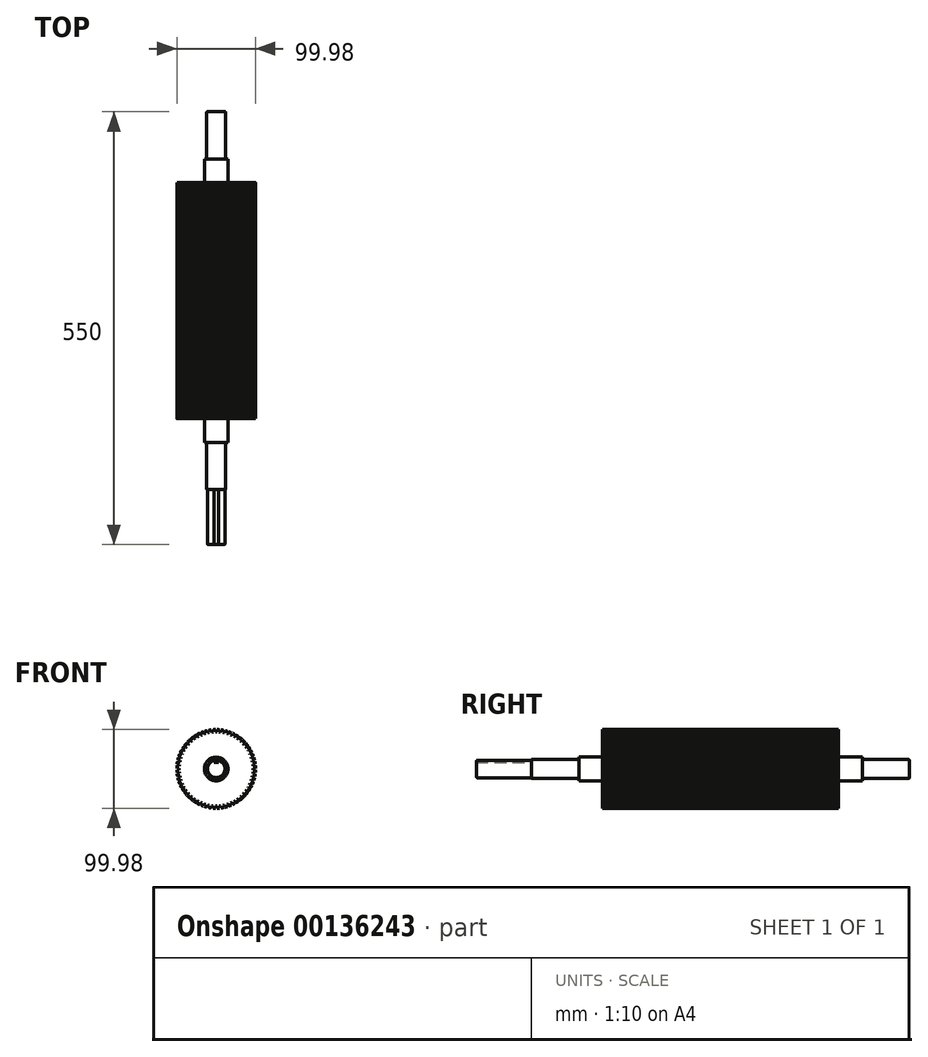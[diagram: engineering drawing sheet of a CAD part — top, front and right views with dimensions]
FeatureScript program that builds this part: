
annotation { "Feature Type Name" : "Feature", "Feature Type Description" : "" }
export const myFeature = defineFeature(function(context is Context, id is Id, definition is map)
    precondition{}
    {
        {
            var Q0;
            Q0=qCreatedBy(makeId("Front.planeOp"),FACE);
            var sketch = newSketch(context, id + "F0", { "sketchPlane" : qUnion([Q0])});
            skCircle(sketch, "E0", {"center": v(0, 0) * mm, "radius": 50 * mm});
            skLineSegment(sketch, "E1.bottom", {"start": v(-1, 50) * mm, "end": v(0, 50) * mm});
            skLineSegment(sketch, "E1.top", {"start": v(-1, 47) * mm, "end": v(0, 47) * mm});
            skLineSegment(sketch, "E1.left", {"start": v(-1, 50) * mm, "end": v(-1, 47) * mm});
            skLineSegment(sketch, "E2.MirrorCS", {"start": v(1, 50) * mm, "end": v(1, 47) * mm});
            skLineSegment(sketch, "E3.MirrorCS", {"start": v(1, 47) * mm, "end": v(0, 47) * mm});
            skPoint(sketch, "E4.MirrorCS.end.orphan", {"position": v(-2, 47) * mm});
            skPoint(sketch, "E4.MirrorCS.start.orphan", {"position": v(-1, 47) * mm});
            skLineSegment(sketch, "E5.1.0", {"start": v(-6.22, 49.62) * mm, "end": v(-5.9, 46.64) * mm});
            skLineSegment(sketch, "E5.1.1", {"start": v(-5.9, 46.64) * mm, "end": v(-4.91, 46.74) * mm});
            skLineSegment(sketch, "E5.1.2", {"start": v(-3.92, 46.85) * mm, "end": v(-4.91, 46.74) * mm});
            skLineSegment(sketch, "E5.1.3", {"start": v(-4.23, 49.83) * mm, "end": v(-3.92, 46.85) * mm});
            skLineSegment(sketch, "E5.2.0", {"start": v(-11.37, 48.7) * mm, "end": v(-10.75, 45.77) * mm});
            skLineSegment(sketch, "E5.2.1", {"start": v(-10.75, 45.77) * mm, "end": v(-9.77, 45.97) * mm});
            skLineSegment(sketch, "E5.2.2", {"start": v(-8.8, 46.18) * mm, "end": v(-9.77, 45.97) * mm});
            skLineSegment(sketch, "E5.2.3", {"start": v(-9.42, 49.12) * mm, "end": v(-8.8, 46.18) * mm});
            skLineSegment(sketch, "E5.3.0", {"start": v(-16.4, 47.24) * mm, "end": v(-15.47, 44.4) * mm});
            skLineSegment(sketch, "E5.3.1", {"start": v(-15.47, 44.4) * mm, "end": v(-14.52, 44.7) * mm});
            skLineSegment(sketch, "E5.3.2", {"start": v(-13.57, 45) * mm, "end": v(-14.52, 44.7) * mm});
            skLineSegment(sketch, "E5.3.3", {"start": v(-14.5, 47.86) * mm, "end": v(-13.57, 45) * mm});
            skLineSegment(sketch, "E5.4.0", {"start": v(-21.25, 45.27) * mm, "end": v(-20.03, 42.53) * mm});
            skLineSegment(sketch, "E5.4.1", {"start": v(-20.03, 42.53) * mm, "end": v(-19.12, 42.94) * mm});
            skLineSegment(sketch, "E5.4.2", {"start": v(-18.2, 43.34) * mm, "end": v(-19.12, 42.94) * mm});
            skLineSegment(sketch, "E5.4.3", {"start": v(-19.42, 46.08) * mm, "end": v(-18.2, 43.34) * mm});
            skLineSegment(sketch, "E5.5.0", {"start": v(-25.87, 42.8) * mm, "end": v(-24.37, 40.2) * mm});
            skLineSegment(sketch, "E5.5.1", {"start": v(-24.37, 40.2) * mm, "end": v(-23.5, 40.7) * mm});
            skLineSegment(sketch, "E5.5.2", {"start": v(-22.63, 41.2) * mm, "end": v(-23.5, 40.7) * mm});
            skLineSegment(sketch, "E5.5.3", {"start": v(-24.13, 43.8) * mm, "end": v(-22.63, 41.2) * mm});
            skLineSegment(sketch, "E5.6.0", {"start": v(-30.2, 39.86) * mm, "end": v(-28.43, 37.44) * mm});
            skLineSegment(sketch, "E5.6.1", {"start": v(-28.43, 37.44) * mm, "end": v(-27.63, 38.02) * mm});
            skLineSegment(sketch, "E5.6.2", {"start": v(-26.82, 38.61) * mm, "end": v(-27.63, 38.02) * mm});
            skLineSegment(sketch, "E5.6.3", {"start": v(-28.58, 41.04) * mm, "end": v(-26.82, 38.61) * mm});
            skLineSegment(sketch, "E5.7.0", {"start": v(-34.2, 36.49) * mm, "end": v(-32.2, 34.26) * mm});
            skLineSegment(sketch, "E5.7.1", {"start": v(-32.2, 34.26) * mm, "end": v(-31.45, 34.93) * mm});
            skLineSegment(sketch, "E5.7.2", {"start": v(-30.7, 35.6) * mm, "end": v(-31.45, 34.93) * mm});
            skLineSegment(sketch, "E5.7.3", {"start": v(-32.71, 37.83) * mm, "end": v(-30.7, 35.6) * mm});
            skLineSegment(sketch, "E5.8.0", {"start": v(-37.83, 32.71) * mm, "end": v(-35.6, 30.7) * mm});
            skLineSegment(sketch, "E5.8.1", {"start": v(-35.6, 30.7) * mm, "end": v(-34.93, 31.45) * mm});
            skLineSegment(sketch, "E5.8.2", {"start": v(-34.26, 32.2) * mm, "end": v(-34.93, 31.45) * mm});
            skLineSegment(sketch, "E5.8.3", {"start": v(-36.49, 34.2) * mm, "end": v(-34.26, 32.2) * mm});
            skLineSegment(sketch, "E5.9.0", {"start": v(-41.04, 28.58) * mm, "end": v(-38.61, 26.82) * mm});
            skLineSegment(sketch, "E5.9.1", {"start": v(-38.61, 26.82) * mm, "end": v(-38.02, 27.63) * mm});
            skLineSegment(sketch, "E5.9.2", {"start": v(-37.44, 28.43) * mm, "end": v(-38.02, 27.63) * mm});
            skLineSegment(sketch, "E5.9.3", {"start": v(-39.86, 30.2) * mm, "end": v(-37.44, 28.43) * mm});
            skLineSegment(sketch, "E5.10.0", {"start": v(-43.8, 24.13) * mm, "end": v(-41.2, 22.63) * mm});
            skLineSegment(sketch, "E5.10.1", {"start": v(-41.2, 22.63) * mm, "end": v(-40.7, 23.5) * mm});
            skLineSegment(sketch, "E5.10.2", {"start": v(-40.2, 24.37) * mm, "end": v(-40.7, 23.5) * mm});
            skLineSegment(sketch, "E5.10.3", {"start": v(-42.8, 25.87) * mm, "end": v(-40.2, 24.37) * mm});
            skLineSegment(sketch, "E5.11.0", {"start": v(-46.08, 19.42) * mm, "end": v(-43.34, 18.2) * mm});
            skLineSegment(sketch, "E5.11.1", {"start": v(-43.34, 18.2) * mm, "end": v(-42.94, 19.12) * mm});
            skLineSegment(sketch, "E5.11.2", {"start": v(-42.53, 20.03) * mm, "end": v(-42.94, 19.12) * mm});
            skLineSegment(sketch, "E5.11.3", {"start": v(-45.27, 21.25) * mm, "end": v(-42.53, 20.03) * mm});
            skLineSegment(sketch, "E5.12.0", {"start": v(-47.86, 14.5) * mm, "end": v(-45, 13.57) * mm});
            skLineSegment(sketch, "E5.12.1", {"start": v(-45, 13.57) * mm, "end": v(-44.7, 14.52) * mm});
            skLineSegment(sketch, "E5.12.2", {"start": v(-44.4, 15.47) * mm, "end": v(-44.7, 14.52) * mm});
            skLineSegment(sketch, "E5.12.3", {"start": v(-47.24, 16.4) * mm, "end": v(-44.4, 15.47) * mm});
            skLineSegment(sketch, "E5.13.0", {"start": v(-49.12, 9.42) * mm, "end": v(-46.18, 8.8) * mm});
            skLineSegment(sketch, "E5.13.1", {"start": v(-46.18, 8.8) * mm, "end": v(-45.97, 9.77) * mm});
            skLineSegment(sketch, "E5.13.2", {"start": v(-45.77, 10.75) * mm, "end": v(-45.97, 9.77) * mm});
            skLineSegment(sketch, "E5.13.3", {"start": v(-48.7, 11.37) * mm, "end": v(-45.77, 10.75) * mm});
            skLineSegment(sketch, "E5.14.0", {"start": v(-49.83, 4.23) * mm, "end": v(-46.85, 3.92) * mm});
            skLineSegment(sketch, "E5.14.1", {"start": v(-46.85, 3.92) * mm, "end": v(-46.74, 4.91) * mm});
            skLineSegment(sketch, "E5.14.2", {"start": v(-46.64, 5.9) * mm, "end": v(-46.74, 4.91) * mm});
            skLineSegment(sketch, "E5.14.3", {"start": v(-49.62, 6.22) * mm, "end": v(-46.64, 5.9) * mm});
            skLineSegment(sketch, "E5.15.0", {"start": v(-50, -1) * mm, "end": v(-47, -1) * mm});
            skLineSegment(sketch, "E5.15.1", {"start": v(-47, -1) * mm, "end": v(-47, 0) * mm});
            skLineSegment(sketch, "E5.15.2", {"start": v(-47, 1) * mm, "end": v(-47, 0) * mm});
            skLineSegment(sketch, "E5.15.3", {"start": v(-50, 1) * mm, "end": v(-47, 1) * mm});
            skLineSegment(sketch, "E5.16.0", {"start": v(-49.62, -6.22) * mm, "end": v(-46.64, -5.9) * mm});
            skLineSegment(sketch, "E5.16.1", {"start": v(-46.64, -5.9) * mm, "end": v(-46.74, -4.91) * mm});
            skLineSegment(sketch, "E5.16.2", {"start": v(-46.85, -3.92) * mm, "end": v(-46.74, -4.91) * mm});
            skLineSegment(sketch, "E5.16.3", {"start": v(-49.83, -4.23) * mm, "end": v(-46.85, -3.92) * mm});
            skLineSegment(sketch, "E5.17.0", {"start": v(-48.7, -11.37) * mm, "end": v(-45.77, -10.75) * mm});
            skLineSegment(sketch, "E5.17.1", {"start": v(-45.77, -10.75) * mm, "end": v(-45.97, -9.77) * mm});
            skLineSegment(sketch, "E5.17.2", {"start": v(-46.18, -8.8) * mm, "end": v(-45.97, -9.77) * mm});
            skLineSegment(sketch, "E5.17.3", {"start": v(-49.12, -9.42) * mm, "end": v(-46.18, -8.8) * mm});
            skLineSegment(sketch, "E5.18.0", {"start": v(-47.24, -16.4) * mm, "end": v(-44.4, -15.47) * mm});
            skLineSegment(sketch, "E5.18.1", {"start": v(-44.4, -15.47) * mm, "end": v(-44.7, -14.52) * mm});
            skLineSegment(sketch, "E5.18.2", {"start": v(-45, -13.57) * mm, "end": v(-44.7, -14.52) * mm});
            skLineSegment(sketch, "E5.18.3", {"start": v(-47.86, -14.5) * mm, "end": v(-45, -13.57) * mm});
            skLineSegment(sketch, "E5.19.0", {"start": v(-45.27, -21.25) * mm, "end": v(-42.53, -20.03) * mm});
            skLineSegment(sketch, "E5.19.1", {"start": v(-42.53, -20.03) * mm, "end": v(-42.94, -19.12) * mm});
            skLineSegment(sketch, "E5.19.2", {"start": v(-43.34, -18.2) * mm, "end": v(-42.94, -19.12) * mm});
            skLineSegment(sketch, "E5.19.3", {"start": v(-46.08, -19.42) * mm, "end": v(-43.34, -18.2) * mm});
            skLineSegment(sketch, "E5.20.0", {"start": v(-42.8, -25.87) * mm, "end": v(-40.2, -24.37) * mm});
            skLineSegment(sketch, "E5.20.1", {"start": v(-40.2, -24.37) * mm, "end": v(-40.7, -23.5) * mm});
            skLineSegment(sketch, "E5.20.2", {"start": v(-41.2, -22.63) * mm, "end": v(-40.7, -23.5) * mm});
            skLineSegment(sketch, "E5.20.3", {"start": v(-43.8, -24.13) * mm, "end": v(-41.2, -22.63) * mm});
            skLineSegment(sketch, "E5.21.0", {"start": v(-39.86, -30.2) * mm, "end": v(-37.44, -28.43) * mm});
            skLineSegment(sketch, "E5.21.1", {"start": v(-37.44, -28.43) * mm, "end": v(-38.02, -27.63) * mm});
            skLineSegment(sketch, "E5.21.2", {"start": v(-38.61, -26.82) * mm, "end": v(-38.02, -27.63) * mm});
            skLineSegment(sketch, "E5.21.3", {"start": v(-41.04, -28.58) * mm, "end": v(-38.61, -26.82) * mm});
            skLineSegment(sketch, "E5.22.0", {"start": v(-36.49, -34.2) * mm, "end": v(-34.26, -32.2) * mm});
            skLineSegment(sketch, "E5.22.1", {"start": v(-34.26, -32.2) * mm, "end": v(-34.93, -31.45) * mm});
            skLineSegment(sketch, "E5.22.2", {"start": v(-35.6, -30.7) * mm, "end": v(-34.93, -31.45) * mm});
            skLineSegment(sketch, "E5.22.3", {"start": v(-37.83, -32.71) * mm, "end": v(-35.6, -30.7) * mm});
            skLineSegment(sketch, "E5.23.0", {"start": v(-32.71, -37.83) * mm, "end": v(-30.7, -35.6) * mm});
            skLineSegment(sketch, "E5.23.1", {"start": v(-30.7, -35.6) * mm, "end": v(-31.45, -34.93) * mm});
            skLineSegment(sketch, "E5.23.2", {"start": v(-32.2, -34.26) * mm, "end": v(-31.45, -34.93) * mm});
            skLineSegment(sketch, "E5.23.3", {"start": v(-34.2, -36.49) * mm, "end": v(-32.2, -34.26) * mm});
            skLineSegment(sketch, "E5.24.0", {"start": v(-28.58, -41.04) * mm, "end": v(-26.82, -38.61) * mm});
            skLineSegment(sketch, "E5.24.1", {"start": v(-26.82, -38.61) * mm, "end": v(-27.63, -38.02) * mm});
            skLineSegment(sketch, "E5.24.2", {"start": v(-28.43, -37.44) * mm, "end": v(-27.63, -38.02) * mm});
            skLineSegment(sketch, "E5.24.3", {"start": v(-30.2, -39.86) * mm, "end": v(-28.43, -37.44) * mm});
            skLineSegment(sketch, "E5.25.0", {"start": v(-24.13, -43.8) * mm, "end": v(-22.63, -41.2) * mm});
            skLineSegment(sketch, "E5.25.1", {"start": v(-22.63, -41.2) * mm, "end": v(-23.5, -40.7) * mm});
            skLineSegment(sketch, "E5.25.2", {"start": v(-24.37, -40.2) * mm, "end": v(-23.5, -40.7) * mm});
            skLineSegment(sketch, "E5.25.3", {"start": v(-25.87, -42.8) * mm, "end": v(-24.37, -40.2) * mm});
            skLineSegment(sketch, "E5.26.0", {"start": v(-19.42, -46.08) * mm, "end": v(-18.2, -43.34) * mm});
            skLineSegment(sketch, "E5.26.1", {"start": v(-18.2, -43.34) * mm, "end": v(-19.12, -42.94) * mm});
            skLineSegment(sketch, "E5.26.2", {"start": v(-20.03, -42.53) * mm, "end": v(-19.12, -42.94) * mm});
            skLineSegment(sketch, "E5.26.3", {"start": v(-21.25, -45.27) * mm, "end": v(-20.03, -42.53) * mm});
            skLineSegment(sketch, "E5.27.0", {"start": v(-14.5, -47.86) * mm, "end": v(-13.57, -45) * mm});
            skLineSegment(sketch, "E5.27.1", {"start": v(-13.57, -45) * mm, "end": v(-14.52, -44.7) * mm});
            skLineSegment(sketch, "E5.27.2", {"start": v(-15.47, -44.4) * mm, "end": v(-14.52, -44.7) * mm});
            skLineSegment(sketch, "E5.27.3", {"start": v(-16.4, -47.24) * mm, "end": v(-15.47, -44.4) * mm});
            skLineSegment(sketch, "E5.28.0", {"start": v(-9.42, -49.12) * mm, "end": v(-8.8, -46.18) * mm});
            skLineSegment(sketch, "E5.28.1", {"start": v(-8.8, -46.18) * mm, "end": v(-9.77, -45.97) * mm});
            skLineSegment(sketch, "E5.28.2", {"start": v(-10.75, -45.77) * mm, "end": v(-9.77, -45.97) * mm});
            skLineSegment(sketch, "E5.28.3", {"start": v(-11.37, -48.7) * mm, "end": v(-10.75, -45.77) * mm});
            skLineSegment(sketch, "E5.29.0", {"start": v(-4.23, -49.83) * mm, "end": v(-3.92, -46.85) * mm});
            skLineSegment(sketch, "E5.29.1", {"start": v(-3.92, -46.85) * mm, "end": v(-4.91, -46.74) * mm});
            skLineSegment(sketch, "E5.29.2", {"start": v(-5.9, -46.64) * mm, "end": v(-4.91, -46.74) * mm});
            skLineSegment(sketch, "E5.29.3", {"start": v(-6.22, -49.62) * mm, "end": v(-5.9, -46.64) * mm});
            skLineSegment(sketch, "E5.30.0", {"start": v(1, -50) * mm, "end": v(1, -47) * mm});
            skLineSegment(sketch, "E5.30.1", {"start": v(1, -47) * mm, "end": v(0, -47) * mm});
            skLineSegment(sketch, "E5.30.2", {"start": v(-1, -47) * mm, "end": v(0, -47) * mm});
            skLineSegment(sketch, "E5.30.3", {"start": v(-1, -50) * mm, "end": v(-1, -47) * mm});
            skLineSegment(sketch, "E5.31.0", {"start": v(6.22, -49.62) * mm, "end": v(5.9, -46.64) * mm});
            skLineSegment(sketch, "E5.31.1", {"start": v(5.9, -46.64) * mm, "end": v(4.91, -46.74) * mm});
            skLineSegment(sketch, "E5.31.2", {"start": v(3.92, -46.85) * mm, "end": v(4.91, -46.74) * mm});
            skLineSegment(sketch, "E5.31.3", {"start": v(4.23, -49.83) * mm, "end": v(3.92, -46.85) * mm});
            skLineSegment(sketch, "E5.32.0", {"start": v(11.37, -48.7) * mm, "end": v(10.75, -45.77) * mm});
            skLineSegment(sketch, "E5.32.1", {"start": v(10.75, -45.77) * mm, "end": v(9.77, -45.97) * mm});
            skLineSegment(sketch, "E5.32.2", {"start": v(8.8, -46.18) * mm, "end": v(9.77, -45.97) * mm});
            skLineSegment(sketch, "E5.32.3", {"start": v(9.42, -49.12) * mm, "end": v(8.8, -46.18) * mm});
            skLineSegment(sketch, "E5.33.0", {"start": v(16.4, -47.24) * mm, "end": v(15.47, -44.4) * mm});
            skLineSegment(sketch, "E5.33.1", {"start": v(15.47, -44.4) * mm, "end": v(14.52, -44.7) * mm});
            skLineSegment(sketch, "E5.33.2", {"start": v(13.57, -45) * mm, "end": v(14.52, -44.7) * mm});
            skLineSegment(sketch, "E5.33.3", {"start": v(14.5, -47.86) * mm, "end": v(13.57, -45) * mm});
            skLineSegment(sketch, "E5.34.0", {"start": v(21.25, -45.27) * mm, "end": v(20.03, -42.53) * mm});
            skLineSegment(sketch, "E5.34.1", {"start": v(20.03, -42.53) * mm, "end": v(19.12, -42.94) * mm});
            skLineSegment(sketch, "E5.34.2", {"start": v(18.2, -43.34) * mm, "end": v(19.12, -42.94) * mm});
            skLineSegment(sketch, "E5.34.3", {"start": v(19.42, -46.08) * mm, "end": v(18.2, -43.34) * mm});
            skLineSegment(sketch, "E5.35.0", {"start": v(25.87, -42.8) * mm, "end": v(24.37, -40.2) * mm});
            skLineSegment(sketch, "E5.35.1", {"start": v(24.37, -40.2) * mm, "end": v(23.5, -40.7) * mm});
            skLineSegment(sketch, "E5.35.2", {"start": v(22.63, -41.2) * mm, "end": v(23.5, -40.7) * mm});
            skLineSegment(sketch, "E5.35.3", {"start": v(24.13, -43.8) * mm, "end": v(22.63, -41.2) * mm});
            skLineSegment(sketch, "E5.36.0", {"start": v(30.2, -39.86) * mm, "end": v(28.43, -37.44) * mm});
            skLineSegment(sketch, "E5.36.1", {"start": v(28.43, -37.44) * mm, "end": v(27.63, -38.02) * mm});
            skLineSegment(sketch, "E5.36.2", {"start": v(26.82, -38.61) * mm, "end": v(27.63, -38.02) * mm});
            skLineSegment(sketch, "E5.36.3", {"start": v(28.58, -41.04) * mm, "end": v(26.82, -38.61) * mm});
            skLineSegment(sketch, "E5.37.0", {"start": v(34.2, -36.49) * mm, "end": v(32.2, -34.26) * mm});
            skLineSegment(sketch, "E5.37.1", {"start": v(32.2, -34.26) * mm, "end": v(31.45, -34.93) * mm});
            skLineSegment(sketch, "E5.37.2", {"start": v(30.7, -35.6) * mm, "end": v(31.45, -34.93) * mm});
            skLineSegment(sketch, "E5.37.3", {"start": v(32.71, -37.83) * mm, "end": v(30.7, -35.6) * mm});
            skLineSegment(sketch, "E5.38.0", {"start": v(37.83, -32.71) * mm, "end": v(35.6, -30.7) * mm});
            skLineSegment(sketch, "E5.38.1", {"start": v(35.6, -30.7) * mm, "end": v(34.93, -31.45) * mm});
            skLineSegment(sketch, "E5.38.2", {"start": v(34.26, -32.2) * mm, "end": v(34.93, -31.45) * mm});
            skLineSegment(sketch, "E5.38.3", {"start": v(36.49, -34.2) * mm, "end": v(34.26, -32.2) * mm});
            skLineSegment(sketch, "E5.39.0", {"start": v(41.04, -28.58) * mm, "end": v(38.61, -26.82) * mm});
            skLineSegment(sketch, "E5.39.1", {"start": v(38.61, -26.82) * mm, "end": v(38.02, -27.63) * mm});
            skLineSegment(sketch, "E5.39.2", {"start": v(37.44, -28.43) * mm, "end": v(38.02, -27.63) * mm});
            skLineSegment(sketch, "E5.39.3", {"start": v(39.86, -30.2) * mm, "end": v(37.44, -28.43) * mm});
            skLineSegment(sketch, "E5.40.0", {"start": v(43.8, -24.13) * mm, "end": v(41.2, -22.63) * mm});
            skLineSegment(sketch, "E5.40.1", {"start": v(41.2, -22.63) * mm, "end": v(40.7, -23.5) * mm});
            skLineSegment(sketch, "E5.40.2", {"start": v(40.2, -24.37) * mm, "end": v(40.7, -23.5) * mm});
            skLineSegment(sketch, "E5.40.3", {"start": v(42.8, -25.87) * mm, "end": v(40.2, -24.37) * mm});
            skLineSegment(sketch, "E5.41.0", {"start": v(46.08, -19.42) * mm, "end": v(43.34, -18.2) * mm});
            skLineSegment(sketch, "E5.41.1", {"start": v(43.34, -18.2) * mm, "end": v(42.94, -19.12) * mm});
            skLineSegment(sketch, "E5.41.2", {"start": v(42.53, -20.03) * mm, "end": v(42.94, -19.12) * mm});
            skLineSegment(sketch, "E5.41.3", {"start": v(45.27, -21.25) * mm, "end": v(42.53, -20.03) * mm});
            skLineSegment(sketch, "E5.42.0", {"start": v(47.86, -14.5) * mm, "end": v(45, -13.57) * mm});
            skLineSegment(sketch, "E5.42.1", {"start": v(45, -13.57) * mm, "end": v(44.7, -14.52) * mm});
            skLineSegment(sketch, "E5.42.2", {"start": v(44.4, -15.47) * mm, "end": v(44.7, -14.52) * mm});
            skLineSegment(sketch, "E5.42.3", {"start": v(47.24, -16.4) * mm, "end": v(44.4, -15.47) * mm});
            skLineSegment(sketch, "E5.43.0", {"start": v(49.12, -9.42) * mm, "end": v(46.18, -8.8) * mm});
            skLineSegment(sketch, "E5.43.1", {"start": v(46.18, -8.8) * mm, "end": v(45.97, -9.77) * mm});
            skLineSegment(sketch, "E5.43.2", {"start": v(45.77, -10.75) * mm, "end": v(45.97, -9.77) * mm});
            skLineSegment(sketch, "E5.43.3", {"start": v(48.7, -11.37) * mm, "end": v(45.77, -10.75) * mm});
            skLineSegment(sketch, "E5.44.0", {"start": v(49.83, -4.23) * mm, "end": v(46.85, -3.92) * mm});
            skLineSegment(sketch, "E5.44.1", {"start": v(46.85, -3.92) * mm, "end": v(46.74, -4.91) * mm});
            skLineSegment(sketch, "E5.44.2", {"start": v(46.64, -5.9) * mm, "end": v(46.74, -4.91) * mm});
            skLineSegment(sketch, "E5.44.3", {"start": v(49.62, -6.22) * mm, "end": v(46.64, -5.9) * mm});
            skLineSegment(sketch, "E5.45.0", {"start": v(50, 1) * mm, "end": v(47, 1) * mm});
            skLineSegment(sketch, "E5.45.1", {"start": v(47, 1) * mm, "end": v(47, 0) * mm});
            skLineSegment(sketch, "E5.45.2", {"start": v(47, -1) * mm, "end": v(47, 0) * mm});
            skLineSegment(sketch, "E5.45.3", {"start": v(50, -1) * mm, "end": v(47, -1) * mm});
            skLineSegment(sketch, "E5.46.0", {"start": v(49.62, 6.22) * mm, "end": v(46.64, 5.9) * mm});
            skLineSegment(sketch, "E5.46.1", {"start": v(46.64, 5.9) * mm, "end": v(46.74, 4.91) * mm});
            skLineSegment(sketch, "E5.46.2", {"start": v(46.85, 3.92) * mm, "end": v(46.74, 4.91) * mm});
            skLineSegment(sketch, "E5.46.3", {"start": v(49.83, 4.23) * mm, "end": v(46.85, 3.92) * mm});
            skLineSegment(sketch, "E5.47.0", {"start": v(48.7, 11.37) * mm, "end": v(45.77, 10.75) * mm});
            skLineSegment(sketch, "E5.47.1", {"start": v(45.77, 10.75) * mm, "end": v(45.97, 9.77) * mm});
            skLineSegment(sketch, "E5.47.2", {"start": v(46.18, 8.8) * mm, "end": v(45.97, 9.77) * mm});
            skLineSegment(sketch, "E5.47.3", {"start": v(49.12, 9.42) * mm, "end": v(46.18, 8.8) * mm});
            skLineSegment(sketch, "E5.48.0", {"start": v(47.24, 16.4) * mm, "end": v(44.4, 15.47) * mm});
            skLineSegment(sketch, "E5.48.1", {"start": v(44.4, 15.47) * mm, "end": v(44.7, 14.52) * mm});
            skLineSegment(sketch, "E5.48.2", {"start": v(45, 13.57) * mm, "end": v(44.7, 14.52) * mm});
            skLineSegment(sketch, "E5.48.3", {"start": v(47.86, 14.5) * mm, "end": v(45, 13.57) * mm});
            skLineSegment(sketch, "E5.49.0", {"start": v(45.27, 21.25) * mm, "end": v(42.53, 20.03) * mm});
            skLineSegment(sketch, "E5.49.1", {"start": v(42.53, 20.03) * mm, "end": v(42.94, 19.12) * mm});
            skLineSegment(sketch, "E5.49.2", {"start": v(43.34, 18.2) * mm, "end": v(42.94, 19.12) * mm});
            skLineSegment(sketch, "E5.49.3", {"start": v(46.08, 19.42) * mm, "end": v(43.34, 18.2) * mm});
            skLineSegment(sketch, "E5.50.0", {"start": v(42.8, 25.87) * mm, "end": v(40.2, 24.37) * mm});
            skLineSegment(sketch, "E5.50.1", {"start": v(40.2, 24.37) * mm, "end": v(40.7, 23.5) * mm});
            skLineSegment(sketch, "E5.50.2", {"start": v(41.2, 22.63) * mm, "end": v(40.7, 23.5) * mm});
            skLineSegment(sketch, "E5.50.3", {"start": v(43.8, 24.13) * mm, "end": v(41.2, 22.63) * mm});
            skLineSegment(sketch, "E5.51.0", {"start": v(39.86, 30.2) * mm, "end": v(37.44, 28.43) * mm});
            skLineSegment(sketch, "E5.51.1", {"start": v(37.44, 28.43) * mm, "end": v(38.02, 27.63) * mm});
            skLineSegment(sketch, "E5.51.2", {"start": v(38.61, 26.82) * mm, "end": v(38.02, 27.63) * mm});
            skLineSegment(sketch, "E5.51.3", {"start": v(41.04, 28.58) * mm, "end": v(38.61, 26.82) * mm});
            skLineSegment(sketch, "E5.52.0", {"start": v(36.49, 34.2) * mm, "end": v(34.26, 32.2) * mm});
            skLineSegment(sketch, "E5.52.1", {"start": v(34.26, 32.2) * mm, "end": v(34.93, 31.45) * mm});
            skLineSegment(sketch, "E5.52.2", {"start": v(35.6, 30.7) * mm, "end": v(34.93, 31.45) * mm});
            skLineSegment(sketch, "E5.52.3", {"start": v(37.83, 32.71) * mm, "end": v(35.6, 30.7) * mm});
            skLineSegment(sketch, "E5.53.0", {"start": v(32.71, 37.83) * mm, "end": v(30.7, 35.6) * mm});
            skLineSegment(sketch, "E5.53.1", {"start": v(30.7, 35.6) * mm, "end": v(31.45, 34.93) * mm});
            skLineSegment(sketch, "E5.53.2", {"start": v(32.2, 34.26) * mm, "end": v(31.45, 34.93) * mm});
            skLineSegment(sketch, "E5.53.3", {"start": v(34.2, 36.49) * mm, "end": v(32.2, 34.26) * mm});
            skLineSegment(sketch, "E5.54.0", {"start": v(28.58, 41.04) * mm, "end": v(26.82, 38.61) * mm});
            skLineSegment(sketch, "E5.54.1", {"start": v(26.82, 38.61) * mm, "end": v(27.63, 38.02) * mm});
            skLineSegment(sketch, "E5.54.2", {"start": v(28.43, 37.44) * mm, "end": v(27.63, 38.02) * mm});
            skLineSegment(sketch, "E5.54.3", {"start": v(30.2, 39.86) * mm, "end": v(28.43, 37.44) * mm});
            skLineSegment(sketch, "E5.55.0", {"start": v(24.13, 43.8) * mm, "end": v(22.63, 41.2) * mm});
            skLineSegment(sketch, "E5.55.1", {"start": v(22.63, 41.2) * mm, "end": v(23.5, 40.7) * mm});
            skLineSegment(sketch, "E5.55.2", {"start": v(24.37, 40.2) * mm, "end": v(23.5, 40.7) * mm});
            skLineSegment(sketch, "E5.55.3", {"start": v(25.87, 42.8) * mm, "end": v(24.37, 40.2) * mm});
            skLineSegment(sketch, "E5.56.0", {"start": v(19.42, 46.08) * mm, "end": v(18.2, 43.34) * mm});
            skLineSegment(sketch, "E5.56.1", {"start": v(18.2, 43.34) * mm, "end": v(19.12, 42.94) * mm});
            skLineSegment(sketch, "E5.56.2", {"start": v(20.03, 42.53) * mm, "end": v(19.12, 42.94) * mm});
            skLineSegment(sketch, "E5.56.3", {"start": v(21.25, 45.27) * mm, "end": v(20.03, 42.53) * mm});
            skLineSegment(sketch, "E5.57.0", {"start": v(14.5, 47.86) * mm, "end": v(13.57, 45) * mm});
            skLineSegment(sketch, "E5.57.1", {"start": v(13.57, 45) * mm, "end": v(14.52, 44.7) * mm});
            skLineSegment(sketch, "E5.57.2", {"start": v(15.47, 44.4) * mm, "end": v(14.52, 44.7) * mm});
            skLineSegment(sketch, "E5.57.3", {"start": v(16.4, 47.24) * mm, "end": v(15.47, 44.4) * mm});
            skLineSegment(sketch, "E5.58.0", {"start": v(9.42, 49.12) * mm, "end": v(8.8, 46.18) * mm});
            skLineSegment(sketch, "E5.58.1", {"start": v(8.8, 46.18) * mm, "end": v(9.77, 45.97) * mm});
            skLineSegment(sketch, "E5.58.2", {"start": v(10.75, 45.77) * mm, "end": v(9.77, 45.97) * mm});
            skLineSegment(sketch, "E5.58.3", {"start": v(11.37, 48.7) * mm, "end": v(10.75, 45.77) * mm});
            skLineSegment(sketch, "E5.59.0", {"start": v(4.23, 49.83) * mm, "end": v(3.92, 46.85) * mm});
            skLineSegment(sketch, "E5.59.1", {"start": v(3.92, 46.85) * mm, "end": v(4.91, 46.74) * mm});
            skLineSegment(sketch, "E5.59.2", {"start": v(5.9, 46.64) * mm, "end": v(4.91, 46.74) * mm});
            skLineSegment(sketch, "E5.59.3", {"start": v(6.22, 49.62) * mm, "end": v(5.9, 46.64) * mm});
            skSolve(sketch);
        }
        {
            var Q0;
            {var subQ173=sQuery(id+"F0.wireOp",EDGE,"E1.top");Q0=makeQuery(id+"F0.imprint","IMPRINT",FACE,{"disambiguationData":[TD([[makeQuery(id+"F0.imprint","IMPRINT",EDGE,{"derivedFrom":subQ173}),-1.0]])]});}
            extrude(context, id + "F1", {"entities" : qUnion([Q0]), "endBound" : BoundingType.SYMMETRIC, "depth" : 300 * mm});
        }
        {
            var Q0;
            Q0=makeQuery(id+"F1.opExtrude","CAP_FACE",FACE,{"disambiguationData":[OSD([sQuery(id+"F0.wireOp",EDGE,"E0"),sQuery(id+"F0.wireOp",EDGE,"E1.top"),sQuery(id+"F0.wireOp",EDGE,"E1.left"),sQuery(id+"F0.wireOp",EDGE,"E2.MirrorCS"),sQuery(id+"F0.wireOp",EDGE,"E3.MirrorCS"),sQuery(id+"F0.wireOp",EDGE,"E5.1.0"),sQuery(id+"F0.wireOp",EDGE,"E5.1.1"),sQuery(id+"F0.wireOp",EDGE,"E5.1.2"),sQuery(id+"F0.wireOp",EDGE,"E5.1.3"),sQuery(id+"F0.wireOp",EDGE,"E5.2.0"),sQuery(id+"F0.wireOp",EDGE,"E5.2.1"),sQuery(id+"F0.wireOp",EDGE,"E5.2.2"),sQuery(id+"F0.wireOp",EDGE,"E5.2.3"),sQuery(id+"F0.wireOp",EDGE,"E5.3.0"),sQuery(id+"F0.wireOp",EDGE,"E5.3.1"),sQuery(id+"F0.wireOp",EDGE,"E5.3.2"),sQuery(id+"F0.wireOp",EDGE,"E5.3.3"),sQuery(id+"F0.wireOp",EDGE,"E5.4.0"),sQuery(id+"F0.wireOp",EDGE,"E5.4.1"),sQuery(id+"F0.wireOp",EDGE,"E5.4.2"),sQuery(id+"F0.wireOp",EDGE,"E5.4.3"),sQuery(id+"F0.wireOp",EDGE,"E5.5.0"),sQuery(id+"F0.wireOp",EDGE,"E5.5.1"),sQuery(id+"F0.wireOp",EDGE,"E5.5.2"),sQuery(id+"F0.wireOp",EDGE,"E5.5.3"),sQuery(id+"F0.wireOp",EDGE,"E5.6.0"),sQuery(id+"F0.wireOp",EDGE,"E5.6.1"),sQuery(id+"F0.wireOp",EDGE,"E5.6.2"),sQuery(id+"F0.wireOp",EDGE,"E5.6.3"),sQuery(id+"F0.wireOp",EDGE,"E5.7.0"),sQuery(id+"F0.wireOp",EDGE,"E5.7.1"),sQuery(id+"F0.wireOp",EDGE,"E5.7.2"),sQuery(id+"F0.wireOp",EDGE,"E5.7.3"),sQuery(id+"F0.wireOp",EDGE,"E5.8.0"),sQuery(id+"F0.wireOp",EDGE,"E5.8.1"),sQuery(id+"F0.wireOp",EDGE,"E5.8.2"),sQuery(id+"F0.wireOp",EDGE,"E5.8.3"),sQuery(id+"F0.wireOp",EDGE,"E5.9.0"),sQuery(id+"F0.wireOp",EDGE,"E5.9.1"),sQuery(id+"F0.wireOp",EDGE,"E5.9.2"),sQuery(id+"F0.wireOp",EDGE,"E5.9.3"),sQuery(id+"F0.wireOp",EDGE,"E5.10.0"),sQuery(id+"F0.wireOp",EDGE,"E5.10.1"),sQuery(id+"F0.wireOp",EDGE,"E5.10.2"),sQuery(id+"F0.wireOp",EDGE,"E5.10.3"),sQuery(id+"F0.wireOp",EDGE,"E5.11.0"),sQuery(id+"F0.wireOp",EDGE,"E5.11.1"),sQuery(id+"F0.wireOp",EDGE,"E5.11.2"),sQuery(id+"F0.wireOp",EDGE,"E5.11.3"),sQuery(id+"F0.wireOp",EDGE,"E5.12.0"),sQuery(id+"F0.wireOp",EDGE,"E5.12.1"),sQuery(id+"F0.wireOp",EDGE,"E5.12.2"),sQuery(id+"F0.wireOp",EDGE,"E5.12.3"),sQuery(id+"F0.wireOp",EDGE,"E5.13.0"),sQuery(id+"F0.wireOp",EDGE,"E5.13.1"),sQuery(id+"F0.wireOp",EDGE,"E5.13.2"),sQuery(id+"F0.wireOp",EDGE,"E5.13.3"),sQuery(id+"F0.wireOp",EDGE,"E5.14.0"),sQuery(id+"F0.wireOp",EDGE,"E5.14.1"),sQuery(id+"F0.wireOp",EDGE,"E5.14.2"),sQuery(id+"F0.wireOp",EDGE,"E5.14.3"),sQuery(id+"F0.wireOp",EDGE,"E5.15.0"),sQuery(id+"F0.wireOp",EDGE,"E5.15.1"),sQuery(id+"F0.wireOp",EDGE,"E5.15.2"),sQuery(id+"F0.wireOp",EDGE,"E5.15.3"),sQuery(id+"F0.wireOp",EDGE,"E5.16.0"),sQuery(id+"F0.wireOp",EDGE,"E5.16.1"),sQuery(id+"F0.wireOp",EDGE,"E5.16.2"),sQuery(id+"F0.wireOp",EDGE,"E5.16.3"),sQuery(id+"F0.wireOp",EDGE,"E5.17.0"),sQuery(id+"F0.wireOp",EDGE,"E5.17.1"),sQuery(id+"F0.wireOp",EDGE,"E5.17.2"),sQuery(id+"F0.wireOp",EDGE,"E5.17.3"),sQuery(id+"F0.wireOp",EDGE,"E5.18.0"),sQuery(id+"F0.wireOp",EDGE,"E5.18.1"),sQuery(id+"F0.wireOp",EDGE,"E5.18.2"),sQuery(id+"F0.wireOp",EDGE,"E5.18.3"),sQuery(id+"F0.wireOp",EDGE,"E5.19.0"),sQuery(id+"F0.wireOp",EDGE,"E5.19.1"),sQuery(id+"F0.wireOp",EDGE,"E5.19.2"),sQuery(id+"F0.wireOp",EDGE,"E5.19.3"),sQuery(id+"F0.wireOp",EDGE,"E5.20.0"),sQuery(id+"F0.wireOp",EDGE,"E5.20.1"),sQuery(id+"F0.wireOp",EDGE,"E5.20.2"),sQuery(id+"F0.wireOp",EDGE,"E5.20.3"),sQuery(id+"F0.wireOp",EDGE,"E5.21.0"),sQuery(id+"F0.wireOp",EDGE,"E5.21.1"),sQuery(id+"F0.wireOp",EDGE,"E5.21.2"),sQuery(id+"F0.wireOp",EDGE,"E5.21.3"),sQuery(id+"F0.wireOp",EDGE,"E5.22.0"),sQuery(id+"F0.wireOp",EDGE,"E5.22.1"),sQuery(id+"F0.wireOp",EDGE,"E5.22.2"),sQuery(id+"F0.wireOp",EDGE,"E5.22.3"),sQuery(id+"F0.wireOp",EDGE,"E5.23.0"),sQuery(id+"F0.wireOp",EDGE,"E5.23.1"),sQuery(id+"F0.wireOp",EDGE,"E5.23.2"),sQuery(id+"F0.wireOp",EDGE,"E5.23.3"),sQuery(id+"F0.wireOp",EDGE,"E5.24.0"),sQuery(id+"F0.wireOp",EDGE,"E5.24.1"),sQuery(id+"F0.wireOp",EDGE,"E5.24.2"),sQuery(id+"F0.wireOp",EDGE,"E5.24.3"),sQuery(id+"F0.wireOp",EDGE,"E5.25.0"),sQuery(id+"F0.wireOp",EDGE,"E5.25.1"),sQuery(id+"F0.wireOp",EDGE,"E5.25.2"),sQuery(id+"F0.wireOp",EDGE,"E5.25.3"),sQuery(id+"F0.wireOp",EDGE,"E5.26.0"),sQuery(id+"F0.wireOp",EDGE,"E5.26.1"),sQuery(id+"F0.wireOp",EDGE,"E5.26.2"),sQuery(id+"F0.wireOp",EDGE,"E5.26.3"),sQuery(id+"F0.wireOp",EDGE,"E5.27.0"),sQuery(id+"F0.wireOp",EDGE,"E5.27.1"),sQuery(id+"F0.wireOp",EDGE,"E5.27.2"),sQuery(id+"F0.wireOp",EDGE,"E5.27.3"),sQuery(id+"F0.wireOp",EDGE,"E5.28.0"),sQuery(id+"F0.wireOp",EDGE,"E5.28.1"),sQuery(id+"F0.wireOp",EDGE,"E5.28.2"),sQuery(id+"F0.wireOp",EDGE,"E5.28.3"),sQuery(id+"F0.wireOp",EDGE,"E5.29.0"),sQuery(id+"F0.wireOp",EDGE,"E5.29.1"),sQuery(id+"F0.wireOp",EDGE,"E5.29.2"),sQuery(id+"F0.wireOp",EDGE,"E5.29.3"),sQuery(id+"F0.wireOp",EDGE,"E5.30.0"),sQuery(id+"F0.wireOp",EDGE,"E5.30.1"),sQuery(id+"F0.wireOp",EDGE,"E5.30.2"),sQuery(id+"F0.wireOp",EDGE,"E5.30.3"),sQuery(id+"F0.wireOp",EDGE,"E5.31.0"),sQuery(id+"F0.wireOp",EDGE,"E5.31.1"),sQuery(id+"F0.wireOp",EDGE,"E5.31.2"),sQuery(id+"F0.wireOp",EDGE,"E5.31.3"),sQuery(id+"F0.wireOp",EDGE,"E5.32.0"),sQuery(id+"F0.wireOp",EDGE,"E5.32.1"),sQuery(id+"F0.wireOp",EDGE,"E5.32.2"),sQuery(id+"F0.wireOp",EDGE,"E5.32.3"),sQuery(id+"F0.wireOp",EDGE,"E5.33.0"),sQuery(id+"F0.wireOp",EDGE,"E5.33.1"),sQuery(id+"F0.wireOp",EDGE,"E5.33.2"),sQuery(id+"F0.wireOp",EDGE,"E5.33.3"),sQuery(id+"F0.wireOp",EDGE,"E5.34.0"),sQuery(id+"F0.wireOp",EDGE,"E5.34.1"),sQuery(id+"F0.wireOp",EDGE,"E5.34.2"),sQuery(id+"F0.wireOp",EDGE,"E5.34.3"),sQuery(id+"F0.wireOp",EDGE,"E5.35.0"),sQuery(id+"F0.wireOp",EDGE,"E5.35.1"),sQuery(id+"F0.wireOp",EDGE,"E5.35.2"),sQuery(id+"F0.wireOp",EDGE,"E5.35.3"),sQuery(id+"F0.wireOp",EDGE,"E5.36.0"),sQuery(id+"F0.wireOp",EDGE,"E5.36.1"),sQuery(id+"F0.wireOp",EDGE,"E5.36.2"),sQuery(id+"F0.wireOp",EDGE,"E5.36.3"),sQuery(id+"F0.wireOp",EDGE,"E5.37.0"),sQuery(id+"F0.wireOp",EDGE,"E5.37.1"),sQuery(id+"F0.wireOp",EDGE,"E5.37.2"),sQuery(id+"F0.wireOp",EDGE,"E5.37.3"),sQuery(id+"F0.wireOp",EDGE,"E5.38.0"),sQuery(id+"F0.wireOp",EDGE,"E5.38.1"),sQuery(id+"F0.wireOp",EDGE,"E5.38.2"),sQuery(id+"F0.wireOp",EDGE,"E5.38.3"),sQuery(id+"F0.wireOp",EDGE,"E5.39.0"),sQuery(id+"F0.wireOp",EDGE,"E5.39.1"),sQuery(id+"F0.wireOp",EDGE,"E5.39.2"),sQuery(id+"F0.wireOp",EDGE,"E5.39.3"),sQuery(id+"F0.wireOp",EDGE,"E5.40.0"),sQuery(id+"F0.wireOp",EDGE,"E5.40.1"),sQuery(id+"F0.wireOp",EDGE,"E5.40.2"),sQuery(id+"F0.wireOp",EDGE,"E5.40.3"),sQuery(id+"F0.wireOp",EDGE,"E5.41.0"),sQuery(id+"F0.wireOp",EDGE,"E5.41.1"),sQuery(id+"F0.wireOp",EDGE,"E5.41.2"),sQuery(id+"F0.wireOp",EDGE,"E5.41.3"),sQuery(id+"F0.wireOp",EDGE,"E5.42.0"),sQuery(id+"F0.wireOp",EDGE,"E5.42.1"),sQuery(id+"F0.wireOp",EDGE,"E5.42.2"),sQuery(id+"F0.wireOp",EDGE,"E5.42.3"),sQuery(id+"F0.wireOp",EDGE,"E5.43.0"),sQuery(id+"F0.wireOp",EDGE,"E5.43.1"),sQuery(id+"F0.wireOp",EDGE,"E5.43.2"),sQuery(id+"F0.wireOp",EDGE,"E5.43.3"),sQuery(id+"F0.wireOp",EDGE,"E5.44.0"),sQuery(id+"F0.wireOp",EDGE,"E5.44.1"),sQuery(id+"F0.wireOp",EDGE,"E5.44.2"),sQuery(id+"F0.wireOp",EDGE,"E5.44.3"),sQuery(id+"F0.wireOp",EDGE,"E5.45.0"),sQuery(id+"F0.wireOp",EDGE,"E5.45.1"),sQuery(id+"F0.wireOp",EDGE,"E5.45.2"),sQuery(id+"F0.wireOp",EDGE,"E5.45.3"),sQuery(id+"F0.wireOp",EDGE,"E5.46.0"),sQuery(id+"F0.wireOp",EDGE,"E5.46.1"),sQuery(id+"F0.wireOp",EDGE,"E5.46.2"),sQuery(id+"F0.wireOp",EDGE,"E5.46.3"),sQuery(id+"F0.wireOp",EDGE,"E5.47.0"),sQuery(id+"F0.wireOp",EDGE,"E5.47.1"),sQuery(id+"F0.wireOp",EDGE,"E5.47.2"),sQuery(id+"F0.wireOp",EDGE,"E5.47.3"),sQuery(id+"F0.wireOp",EDGE,"E5.48.0"),sQuery(id+"F0.wireOp",EDGE,"E5.48.1"),sQuery(id+"F0.wireOp",EDGE,"E5.48.2"),sQuery(id+"F0.wireOp",EDGE,"E5.48.3"),sQuery(id+"F0.wireOp",EDGE,"E5.49.0"),sQuery(id+"F0.wireOp",EDGE,"E5.49.1"),sQuery(id+"F0.wireOp",EDGE,"E5.49.2"),sQuery(id+"F0.wireOp",EDGE,"E5.49.3"),sQuery(id+"F0.wireOp",EDGE,"E5.50.0"),sQuery(id+"F0.wireOp",EDGE,"E5.50.1"),sQuery(id+"F0.wireOp",EDGE,"E5.50.2"),sQuery(id+"F0.wireOp",EDGE,"E5.50.3"),sQuery(id+"F0.wireOp",EDGE,"E5.51.0"),sQuery(id+"F0.wireOp",EDGE,"E5.51.1"),sQuery(id+"F0.wireOp",EDGE,"E5.51.2"),sQuery(id+"F0.wireOp",EDGE,"E5.51.3"),sQuery(id+"F0.wireOp",EDGE,"E5.52.0"),sQuery(id+"F0.wireOp",EDGE,"E5.52.1"),sQuery(id+"F0.wireOp",EDGE,"E5.52.2"),sQuery(id+"F0.wireOp",EDGE,"E5.52.3"),sQuery(id+"F0.wireOp",EDGE,"E5.53.0"),sQuery(id+"F0.wireOp",EDGE,"E5.53.1"),sQuery(id+"F0.wireOp",EDGE,"E5.53.2"),sQuery(id+"F0.wireOp",EDGE,"E5.53.3"),sQuery(id+"F0.wireOp",EDGE,"E5.54.0"),sQuery(id+"F0.wireOp",EDGE,"E5.54.1"),sQuery(id+"F0.wireOp",EDGE,"E5.54.2"),sQuery(id+"F0.wireOp",EDGE,"E5.54.3"),sQuery(id+"F0.wireOp",EDGE,"E5.55.0"),sQuery(id+"F0.wireOp",EDGE,"E5.55.1"),sQuery(id+"F0.wireOp",EDGE,"E5.55.2"),sQuery(id+"F0.wireOp",EDGE,"E5.55.3"),sQuery(id+"F0.wireOp",EDGE,"E5.56.0"),sQuery(id+"F0.wireOp",EDGE,"E5.56.1"),sQuery(id+"F0.wireOp",EDGE,"E5.56.2"),sQuery(id+"F0.wireOp",EDGE,"E5.56.3"),sQuery(id+"F0.wireOp",EDGE,"E5.57.0"),sQuery(id+"F0.wireOp",EDGE,"E5.57.1"),sQuery(id+"F0.wireOp",EDGE,"E5.57.2"),sQuery(id+"F0.wireOp",EDGE,"E5.57.3"),sQuery(id+"F0.wireOp",EDGE,"E5.58.0"),sQuery(id+"F0.wireOp",EDGE,"E5.58.1"),sQuery(id+"F0.wireOp",EDGE,"E5.58.2"),sQuery(id+"F0.wireOp",EDGE,"E5.58.3"),sQuery(id+"F0.wireOp",EDGE,"E5.59.0"),sQuery(id+"F0.wireOp",EDGE,"E5.59.1"),sQuery(id+"F0.wireOp",EDGE,"E5.59.2"),sQuery(id+"F0.wireOp",EDGE,"E5.59.3")])],"isStart":true});
            var sketch = newSketch(context, id + "F2", { "sketchPlane" : qUnion([Q0])});
            skCircle(sketch, "E6", {"center": v(0, 0) * mm, "radius": 15 * mm});
            skSolve(sketch);
        }
        {
            var Q0;
            Q0 = qSketchRegion(id + "F2", true);
            var Q1;
            Q1=makeQuery(id+"F2.imprint","IMPRINT",FACE,{"disambiguationData":[TD([[makeQuery(id+"F2.imprint","IMPRINT",EDGE,{"derivedFrom":sQuery(id+"F2.wireOp",EDGE,"E6")}),1.0]])]});
            extrude(context, id + "F3", {"entities" : qUnion([Q0, Q1]), "operationType" : NewBodyOperationType.ADD, "depth" : 30 * mm});
        }
        {
            var Q0;
            Q0=makeQuery(id+"F1.opExtrude","SWEPT_BODY",BODY,{"disambiguationData":[OSD([sQuery(id+"F0.wireOp",EDGE,"E0"),sQuery(id+"F0.wireOp",EDGE,"E1.top"),sQuery(id+"F0.wireOp",EDGE,"E1.left"),sQuery(id+"F0.wireOp",EDGE,"E2.MirrorCS"),sQuery(id+"F0.wireOp",EDGE,"E3.MirrorCS"),sQuery(id+"F0.wireOp",EDGE,"E5.1.0"),sQuery(id+"F0.wireOp",EDGE,"E5.1.1"),sQuery(id+"F0.wireOp",EDGE,"E5.1.2"),sQuery(id+"F0.wireOp",EDGE,"E5.1.3"),sQuery(id+"F0.wireOp",EDGE,"E5.2.0"),sQuery(id+"F0.wireOp",EDGE,"E5.2.1"),sQuery(id+"F0.wireOp",EDGE,"E5.2.2"),sQuery(id+"F0.wireOp",EDGE,"E5.2.3"),sQuery(id+"F0.wireOp",EDGE,"E5.3.0"),sQuery(id+"F0.wireOp",EDGE,"E5.3.1"),sQuery(id+"F0.wireOp",EDGE,"E5.3.2"),sQuery(id+"F0.wireOp",EDGE,"E5.3.3"),sQuery(id+"F0.wireOp",EDGE,"E5.4.0"),sQuery(id+"F0.wireOp",EDGE,"E5.4.1"),sQuery(id+"F0.wireOp",EDGE,"E5.4.2"),sQuery(id+"F0.wireOp",EDGE,"E5.4.3"),sQuery(id+"F0.wireOp",EDGE,"E5.5.0"),sQuery(id+"F0.wireOp",EDGE,"E5.5.1"),sQuery(id+"F0.wireOp",EDGE,"E5.5.2"),sQuery(id+"F0.wireOp",EDGE,"E5.5.3"),sQuery(id+"F0.wireOp",EDGE,"E5.6.0"),sQuery(id+"F0.wireOp",EDGE,"E5.6.1"),sQuery(id+"F0.wireOp",EDGE,"E5.6.2"),sQuery(id+"F0.wireOp",EDGE,"E5.6.3"),sQuery(id+"F0.wireOp",EDGE,"E5.7.0"),sQuery(id+"F0.wireOp",EDGE,"E5.7.1"),sQuery(id+"F0.wireOp",EDGE,"E5.7.2"),sQuery(id+"F0.wireOp",EDGE,"E5.7.3"),sQuery(id+"F0.wireOp",EDGE,"E5.8.0"),sQuery(id+"F0.wireOp",EDGE,"E5.8.1"),sQuery(id+"F0.wireOp",EDGE,"E5.8.2"),sQuery(id+"F0.wireOp",EDGE,"E5.8.3"),sQuery(id+"F0.wireOp",EDGE,"E5.9.0"),sQuery(id+"F0.wireOp",EDGE,"E5.9.1"),sQuery(id+"F0.wireOp",EDGE,"E5.9.2"),sQuery(id+"F0.wireOp",EDGE,"E5.9.3"),sQuery(id+"F0.wireOp",EDGE,"E5.10.0"),sQuery(id+"F0.wireOp",EDGE,"E5.10.1"),sQuery(id+"F0.wireOp",EDGE,"E5.10.2"),sQuery(id+"F0.wireOp",EDGE,"E5.10.3"),sQuery(id+"F0.wireOp",EDGE,"E5.11.0"),sQuery(id+"F0.wireOp",EDGE,"E5.11.1"),sQuery(id+"F0.wireOp",EDGE,"E5.11.2"),sQuery(id+"F0.wireOp",EDGE,"E5.11.3"),sQuery(id+"F0.wireOp",EDGE,"E5.12.0"),sQuery(id+"F0.wireOp",EDGE,"E5.12.1"),sQuery(id+"F0.wireOp",EDGE,"E5.12.2"),sQuery(id+"F0.wireOp",EDGE,"E5.12.3"),sQuery(id+"F0.wireOp",EDGE,"E5.13.0"),sQuery(id+"F0.wireOp",EDGE,"E5.13.1"),sQuery(id+"F0.wireOp",EDGE,"E5.13.2"),sQuery(id+"F0.wireOp",EDGE,"E5.13.3"),sQuery(id+"F0.wireOp",EDGE,"E5.14.0"),sQuery(id+"F0.wireOp",EDGE,"E5.14.1"),sQuery(id+"F0.wireOp",EDGE,"E5.14.2"),sQuery(id+"F0.wireOp",EDGE,"E5.14.3"),sQuery(id+"F0.wireOp",EDGE,"E5.15.0"),sQuery(id+"F0.wireOp",EDGE,"E5.15.1"),sQuery(id+"F0.wireOp",EDGE,"E5.15.2"),sQuery(id+"F0.wireOp",EDGE,"E5.15.3"),sQuery(id+"F0.wireOp",EDGE,"E5.16.0"),sQuery(id+"F0.wireOp",EDGE,"E5.16.1"),sQuery(id+"F0.wireOp",EDGE,"E5.16.2"),sQuery(id+"F0.wireOp",EDGE,"E5.16.3"),sQuery(id+"F0.wireOp",EDGE,"E5.17.0"),sQuery(id+"F0.wireOp",EDGE,"E5.17.1"),sQuery(id+"F0.wireOp",EDGE,"E5.17.2"),sQuery(id+"F0.wireOp",EDGE,"E5.17.3"),sQuery(id+"F0.wireOp",EDGE,"E5.18.0"),sQuery(id+"F0.wireOp",EDGE,"E5.18.1"),sQuery(id+"F0.wireOp",EDGE,"E5.18.2"),sQuery(id+"F0.wireOp",EDGE,"E5.18.3"),sQuery(id+"F0.wireOp",EDGE,"E5.19.0"),sQuery(id+"F0.wireOp",EDGE,"E5.19.1"),sQuery(id+"F0.wireOp",EDGE,"E5.19.2"),sQuery(id+"F0.wireOp",EDGE,"E5.19.3"),sQuery(id+"F0.wireOp",EDGE,"E5.20.0"),sQuery(id+"F0.wireOp",EDGE,"E5.20.1"),sQuery(id+"F0.wireOp",EDGE,"E5.20.2"),sQuery(id+"F0.wireOp",EDGE,"E5.20.3"),sQuery(id+"F0.wireOp",EDGE,"E5.21.0"),sQuery(id+"F0.wireOp",EDGE,"E5.21.1"),sQuery(id+"F0.wireOp",EDGE,"E5.21.2"),sQuery(id+"F0.wireOp",EDGE,"E5.21.3"),sQuery(id+"F0.wireOp",EDGE,"E5.22.0"),sQuery(id+"F0.wireOp",EDGE,"E5.22.1"),sQuery(id+"F0.wireOp",EDGE,"E5.22.2"),sQuery(id+"F0.wireOp",EDGE,"E5.22.3"),sQuery(id+"F0.wireOp",EDGE,"E5.23.0"),sQuery(id+"F0.wireOp",EDGE,"E5.23.1"),sQuery(id+"F0.wireOp",EDGE,"E5.23.2"),sQuery(id+"F0.wireOp",EDGE,"E5.23.3"),sQuery(id+"F0.wireOp",EDGE,"E5.24.0"),sQuery(id+"F0.wireOp",EDGE,"E5.24.1"),sQuery(id+"F0.wireOp",EDGE,"E5.24.2"),sQuery(id+"F0.wireOp",EDGE,"E5.24.3"),sQuery(id+"F0.wireOp",EDGE,"E5.25.0"),sQuery(id+"F0.wireOp",EDGE,"E5.25.1"),sQuery(id+"F0.wireOp",EDGE,"E5.25.2"),sQuery(id+"F0.wireOp",EDGE,"E5.25.3"),sQuery(id+"F0.wireOp",EDGE,"E5.26.0"),sQuery(id+"F0.wireOp",EDGE,"E5.26.1"),sQuery(id+"F0.wireOp",EDGE,"E5.26.2"),sQuery(id+"F0.wireOp",EDGE,"E5.26.3"),sQuery(id+"F0.wireOp",EDGE,"E5.27.0"),sQuery(id+"F0.wireOp",EDGE,"E5.27.1"),sQuery(id+"F0.wireOp",EDGE,"E5.27.2"),sQuery(id+"F0.wireOp",EDGE,"E5.27.3"),sQuery(id+"F0.wireOp",EDGE,"E5.28.0"),sQuery(id+"F0.wireOp",EDGE,"E5.28.1"),sQuery(id+"F0.wireOp",EDGE,"E5.28.2"),sQuery(id+"F0.wireOp",EDGE,"E5.28.3"),sQuery(id+"F0.wireOp",EDGE,"E5.29.0"),sQuery(id+"F0.wireOp",EDGE,"E5.29.1"),sQuery(id+"F0.wireOp",EDGE,"E5.29.2"),sQuery(id+"F0.wireOp",EDGE,"E5.29.3"),sQuery(id+"F0.wireOp",EDGE,"E5.30.0"),sQuery(id+"F0.wireOp",EDGE,"E5.30.1"),sQuery(id+"F0.wireOp",EDGE,"E5.30.2"),sQuery(id+"F0.wireOp",EDGE,"E5.30.3"),sQuery(id+"F0.wireOp",EDGE,"E5.31.0"),sQuery(id+"F0.wireOp",EDGE,"E5.31.1"),sQuery(id+"F0.wireOp",EDGE,"E5.31.2"),sQuery(id+"F0.wireOp",EDGE,"E5.31.3"),sQuery(id+"F0.wireOp",EDGE,"E5.32.0"),sQuery(id+"F0.wireOp",EDGE,"E5.32.1"),sQuery(id+"F0.wireOp",EDGE,"E5.32.2"),sQuery(id+"F0.wireOp",EDGE,"E5.32.3"),sQuery(id+"F0.wireOp",EDGE,"E5.33.0"),sQuery(id+"F0.wireOp",EDGE,"E5.33.1"),sQuery(id+"F0.wireOp",EDGE,"E5.33.2"),sQuery(id+"F0.wireOp",EDGE,"E5.33.3"),sQuery(id+"F0.wireOp",EDGE,"E5.34.0"),sQuery(id+"F0.wireOp",EDGE,"E5.34.1"),sQuery(id+"F0.wireOp",EDGE,"E5.34.2"),sQuery(id+"F0.wireOp",EDGE,"E5.34.3"),sQuery(id+"F0.wireOp",EDGE,"E5.35.0"),sQuery(id+"F0.wireOp",EDGE,"E5.35.1"),sQuery(id+"F0.wireOp",EDGE,"E5.35.2"),sQuery(id+"F0.wireOp",EDGE,"E5.35.3"),sQuery(id+"F0.wireOp",EDGE,"E5.36.0"),sQuery(id+"F0.wireOp",EDGE,"E5.36.1"),sQuery(id+"F0.wireOp",EDGE,"E5.36.2"),sQuery(id+"F0.wireOp",EDGE,"E5.36.3"),sQuery(id+"F0.wireOp",EDGE,"E5.37.0"),sQuery(id+"F0.wireOp",EDGE,"E5.37.1"),sQuery(id+"F0.wireOp",EDGE,"E5.37.2"),sQuery(id+"F0.wireOp",EDGE,"E5.37.3"),sQuery(id+"F0.wireOp",EDGE,"E5.38.0"),sQuery(id+"F0.wireOp",EDGE,"E5.38.1"),sQuery(id+"F0.wireOp",EDGE,"E5.38.2"),sQuery(id+"F0.wireOp",EDGE,"E5.38.3"),sQuery(id+"F0.wireOp",EDGE,"E5.39.0"),sQuery(id+"F0.wireOp",EDGE,"E5.39.1"),sQuery(id+"F0.wireOp",EDGE,"E5.39.2"),sQuery(id+"F0.wireOp",EDGE,"E5.39.3"),sQuery(id+"F0.wireOp",EDGE,"E5.40.0"),sQuery(id+"F0.wireOp",EDGE,"E5.40.1"),sQuery(id+"F0.wireOp",EDGE,"E5.40.2"),sQuery(id+"F0.wireOp",EDGE,"E5.40.3"),sQuery(id+"F0.wireOp",EDGE,"E5.41.0"),sQuery(id+"F0.wireOp",EDGE,"E5.41.1"),sQuery(id+"F0.wireOp",EDGE,"E5.41.2"),sQuery(id+"F0.wireOp",EDGE,"E5.41.3"),sQuery(id+"F0.wireOp",EDGE,"E5.42.0"),sQuery(id+"F0.wireOp",EDGE,"E5.42.1"),sQuery(id+"F0.wireOp",EDGE,"E5.42.2"),sQuery(id+"F0.wireOp",EDGE,"E5.42.3"),sQuery(id+"F0.wireOp",EDGE,"E5.43.0"),sQuery(id+"F0.wireOp",EDGE,"E5.43.1"),sQuery(id+"F0.wireOp",EDGE,"E5.43.2"),sQuery(id+"F0.wireOp",EDGE,"E5.43.3"),sQuery(id+"F0.wireOp",EDGE,"E5.44.0"),sQuery(id+"F0.wireOp",EDGE,"E5.44.1"),sQuery(id+"F0.wireOp",EDGE,"E5.44.2"),sQuery(id+"F0.wireOp",EDGE,"E5.44.3"),sQuery(id+"F0.wireOp",EDGE,"E5.45.0"),sQuery(id+"F0.wireOp",EDGE,"E5.45.1"),sQuery(id+"F0.wireOp",EDGE,"E5.45.2"),sQuery(id+"F0.wireOp",EDGE,"E5.45.3"),sQuery(id+"F0.wireOp",EDGE,"E5.46.0"),sQuery(id+"F0.wireOp",EDGE,"E5.46.1"),sQuery(id+"F0.wireOp",EDGE,"E5.46.2"),sQuery(id+"F0.wireOp",EDGE,"E5.46.3"),sQuery(id+"F0.wireOp",EDGE,"E5.47.0"),sQuery(id+"F0.wireOp",EDGE,"E5.47.1"),sQuery(id+"F0.wireOp",EDGE,"E5.47.2"),sQuery(id+"F0.wireOp",EDGE,"E5.47.3"),sQuery(id+"F0.wireOp",EDGE,"E5.48.0"),sQuery(id+"F0.wireOp",EDGE,"E5.48.1"),sQuery(id+"F0.wireOp",EDGE,"E5.48.2"),sQuery(id+"F0.wireOp",EDGE,"E5.48.3"),sQuery(id+"F0.wireOp",EDGE,"E5.49.0"),sQuery(id+"F0.wireOp",EDGE,"E5.49.1"),sQuery(id+"F0.wireOp",EDGE,"E5.49.2"),sQuery(id+"F0.wireOp",EDGE,"E5.49.3"),sQuery(id+"F0.wireOp",EDGE,"E5.50.0"),sQuery(id+"F0.wireOp",EDGE,"E5.50.1"),sQuery(id+"F0.wireOp",EDGE,"E5.50.2"),sQuery(id+"F0.wireOp",EDGE,"E5.50.3"),sQuery(id+"F0.wireOp",EDGE,"E5.51.0"),sQuery(id+"F0.wireOp",EDGE,"E5.51.1"),sQuery(id+"F0.wireOp",EDGE,"E5.51.2"),sQuery(id+"F0.wireOp",EDGE,"E5.51.3"),sQuery(id+"F0.wireOp",EDGE,"E5.52.0"),sQuery(id+"F0.wireOp",EDGE,"E5.52.1"),sQuery(id+"F0.wireOp",EDGE,"E5.52.2"),sQuery(id+"F0.wireOp",EDGE,"E5.52.3"),sQuery(id+"F0.wireOp",EDGE,"E5.53.0"),sQuery(id+"F0.wireOp",EDGE,"E5.53.1"),sQuery(id+"F0.wireOp",EDGE,"E5.53.2"),sQuery(id+"F0.wireOp",EDGE,"E5.53.3"),sQuery(id+"F0.wireOp",EDGE,"E5.54.0"),sQuery(id+"F0.wireOp",EDGE,"E5.54.1"),sQuery(id+"F0.wireOp",EDGE,"E5.54.2"),sQuery(id+"F0.wireOp",EDGE,"E5.54.3"),sQuery(id+"F0.wireOp",EDGE,"E5.55.0"),sQuery(id+"F0.wireOp",EDGE,"E5.55.1"),sQuery(id+"F0.wireOp",EDGE,"E5.55.2"),sQuery(id+"F0.wireOp",EDGE,"E5.55.3"),sQuery(id+"F0.wireOp",EDGE,"E5.56.0"),sQuery(id+"F0.wireOp",EDGE,"E5.56.1"),sQuery(id+"F0.wireOp",EDGE,"E5.56.2"),sQuery(id+"F0.wireOp",EDGE,"E5.56.3"),sQuery(id+"F0.wireOp",EDGE,"E5.57.0"),sQuery(id+"F0.wireOp",EDGE,"E5.57.1"),sQuery(id+"F0.wireOp",EDGE,"E5.57.2"),sQuery(id+"F0.wireOp",EDGE,"E5.57.3"),sQuery(id+"F0.wireOp",EDGE,"E5.58.0"),sQuery(id+"F0.wireOp",EDGE,"E5.58.1"),sQuery(id+"F0.wireOp",EDGE,"E5.58.2"),sQuery(id+"F0.wireOp",EDGE,"E5.58.3"),sQuery(id+"F0.wireOp",EDGE,"E5.59.0"),sQuery(id+"F0.wireOp",EDGE,"E5.59.1"),sQuery(id+"F0.wireOp",EDGE,"E5.59.2"),sQuery(id+"F0.wireOp",EDGE,"E5.59.3")])]});
            var Q1;
            Q1=qCreatedBy(makeId("Front.planeOp"),FACE);
            mirror(context, id + "F4", {"operationType" : NewBodyOperationType.ADD, "entities" : qUnion([Q0]), "mirrorPlane" : qUnion([Q1])});
        }
        {
            var Q0;
            Q0=makeQuery(id+"F4.opPattern","COPY",FACE,{"derivedFrom":makeQuery(id+"F3.opExtrude","CAP_FACE",FACE,{"disambiguationData":[OSD([sQuery(id+"F2.wireOp",EDGE,"E6")])],"isStart":false}),"instanceName":"1"});
            var sketch = newSketch(context, id + "F5", { "sketchPlane" : qUnion([Q0])});
            skCircle(sketch, "E7", {"center": v(0, 0) * mm, "radius": 12 * mm});
            skSolve(sketch);
        }
        {
            var Q0;
            Q0=makeQuery(id+"F5.imprint","IMPRINT",FACE,{"disambiguationData":[TD([[makeQuery(id+"F5.imprint","IMPRINT",EDGE,{"derivedFrom":sQuery(id+"F5.wireOp",EDGE,"E7")}),1.0]])]});
            extrude(context, id + "F6", {"entities" : qUnion([Q0]), "operationType" : NewBodyOperationType.ADD, "depth" : 60 * mm});
        }
        {
            var Q0;
            Q0=makeQuery(id+"F1.opExtrude","SWEPT_BODY",BODY,{"disambiguationData":[OSD([sQuery(id+"F0.wireOp",EDGE,"E0"),sQuery(id+"F0.wireOp",EDGE,"E1.top"),sQuery(id+"F0.wireOp",EDGE,"E1.left"),sQuery(id+"F0.wireOp",EDGE,"E2.MirrorCS"),sQuery(id+"F0.wireOp",EDGE,"E3.MirrorCS"),sQuery(id+"F0.wireOp",EDGE,"E5.1.0"),sQuery(id+"F0.wireOp",EDGE,"E5.1.1"),sQuery(id+"F0.wireOp",EDGE,"E5.1.2"),sQuery(id+"F0.wireOp",EDGE,"E5.1.3"),sQuery(id+"F0.wireOp",EDGE,"E5.2.0"),sQuery(id+"F0.wireOp",EDGE,"E5.2.1"),sQuery(id+"F0.wireOp",EDGE,"E5.2.2"),sQuery(id+"F0.wireOp",EDGE,"E5.2.3"),sQuery(id+"F0.wireOp",EDGE,"E5.3.0"),sQuery(id+"F0.wireOp",EDGE,"E5.3.1"),sQuery(id+"F0.wireOp",EDGE,"E5.3.2"),sQuery(id+"F0.wireOp",EDGE,"E5.3.3"),sQuery(id+"F0.wireOp",EDGE,"E5.4.0"),sQuery(id+"F0.wireOp",EDGE,"E5.4.1"),sQuery(id+"F0.wireOp",EDGE,"E5.4.2"),sQuery(id+"F0.wireOp",EDGE,"E5.4.3"),sQuery(id+"F0.wireOp",EDGE,"E5.5.0"),sQuery(id+"F0.wireOp",EDGE,"E5.5.1"),sQuery(id+"F0.wireOp",EDGE,"E5.5.2"),sQuery(id+"F0.wireOp",EDGE,"E5.5.3"),sQuery(id+"F0.wireOp",EDGE,"E5.6.0"),sQuery(id+"F0.wireOp",EDGE,"E5.6.1"),sQuery(id+"F0.wireOp",EDGE,"E5.6.2"),sQuery(id+"F0.wireOp",EDGE,"E5.6.3"),sQuery(id+"F0.wireOp",EDGE,"E5.7.0"),sQuery(id+"F0.wireOp",EDGE,"E5.7.1"),sQuery(id+"F0.wireOp",EDGE,"E5.7.2"),sQuery(id+"F0.wireOp",EDGE,"E5.7.3"),sQuery(id+"F0.wireOp",EDGE,"E5.8.0"),sQuery(id+"F0.wireOp",EDGE,"E5.8.1"),sQuery(id+"F0.wireOp",EDGE,"E5.8.2"),sQuery(id+"F0.wireOp",EDGE,"E5.8.3"),sQuery(id+"F0.wireOp",EDGE,"E5.9.0"),sQuery(id+"F0.wireOp",EDGE,"E5.9.1"),sQuery(id+"F0.wireOp",EDGE,"E5.9.2"),sQuery(id+"F0.wireOp",EDGE,"E5.9.3"),sQuery(id+"F0.wireOp",EDGE,"E5.10.0"),sQuery(id+"F0.wireOp",EDGE,"E5.10.1"),sQuery(id+"F0.wireOp",EDGE,"E5.10.2"),sQuery(id+"F0.wireOp",EDGE,"E5.10.3"),sQuery(id+"F0.wireOp",EDGE,"E5.11.0"),sQuery(id+"F0.wireOp",EDGE,"E5.11.1"),sQuery(id+"F0.wireOp",EDGE,"E5.11.2"),sQuery(id+"F0.wireOp",EDGE,"E5.11.3"),sQuery(id+"F0.wireOp",EDGE,"E5.12.0"),sQuery(id+"F0.wireOp",EDGE,"E5.12.1"),sQuery(id+"F0.wireOp",EDGE,"E5.12.2"),sQuery(id+"F0.wireOp",EDGE,"E5.12.3"),sQuery(id+"F0.wireOp",EDGE,"E5.13.0"),sQuery(id+"F0.wireOp",EDGE,"E5.13.1"),sQuery(id+"F0.wireOp",EDGE,"E5.13.2"),sQuery(id+"F0.wireOp",EDGE,"E5.13.3"),sQuery(id+"F0.wireOp",EDGE,"E5.14.0"),sQuery(id+"F0.wireOp",EDGE,"E5.14.1"),sQuery(id+"F0.wireOp",EDGE,"E5.14.2"),sQuery(id+"F0.wireOp",EDGE,"E5.14.3"),sQuery(id+"F0.wireOp",EDGE,"E5.15.0"),sQuery(id+"F0.wireOp",EDGE,"E5.15.1"),sQuery(id+"F0.wireOp",EDGE,"E5.15.2"),sQuery(id+"F0.wireOp",EDGE,"E5.15.3"),sQuery(id+"F0.wireOp",EDGE,"E5.16.0"),sQuery(id+"F0.wireOp",EDGE,"E5.16.1"),sQuery(id+"F0.wireOp",EDGE,"E5.16.2"),sQuery(id+"F0.wireOp",EDGE,"E5.16.3"),sQuery(id+"F0.wireOp",EDGE,"E5.17.0"),sQuery(id+"F0.wireOp",EDGE,"E5.17.1"),sQuery(id+"F0.wireOp",EDGE,"E5.17.2"),sQuery(id+"F0.wireOp",EDGE,"E5.17.3"),sQuery(id+"F0.wireOp",EDGE,"E5.18.0"),sQuery(id+"F0.wireOp",EDGE,"E5.18.1"),sQuery(id+"F0.wireOp",EDGE,"E5.18.2"),sQuery(id+"F0.wireOp",EDGE,"E5.18.3"),sQuery(id+"F0.wireOp",EDGE,"E5.19.0"),sQuery(id+"F0.wireOp",EDGE,"E5.19.1"),sQuery(id+"F0.wireOp",EDGE,"E5.19.2"),sQuery(id+"F0.wireOp",EDGE,"E5.19.3"),sQuery(id+"F0.wireOp",EDGE,"E5.20.0"),sQuery(id+"F0.wireOp",EDGE,"E5.20.1"),sQuery(id+"F0.wireOp",EDGE,"E5.20.2"),sQuery(id+"F0.wireOp",EDGE,"E5.20.3"),sQuery(id+"F0.wireOp",EDGE,"E5.21.0"),sQuery(id+"F0.wireOp",EDGE,"E5.21.1"),sQuery(id+"F0.wireOp",EDGE,"E5.21.2"),sQuery(id+"F0.wireOp",EDGE,"E5.21.3"),sQuery(id+"F0.wireOp",EDGE,"E5.22.0"),sQuery(id+"F0.wireOp",EDGE,"E5.22.1"),sQuery(id+"F0.wireOp",EDGE,"E5.22.2"),sQuery(id+"F0.wireOp",EDGE,"E5.22.3"),sQuery(id+"F0.wireOp",EDGE,"E5.23.0"),sQuery(id+"F0.wireOp",EDGE,"E5.23.1"),sQuery(id+"F0.wireOp",EDGE,"E5.23.2"),sQuery(id+"F0.wireOp",EDGE,"E5.23.3"),sQuery(id+"F0.wireOp",EDGE,"E5.24.0"),sQuery(id+"F0.wireOp",EDGE,"E5.24.1"),sQuery(id+"F0.wireOp",EDGE,"E5.24.2"),sQuery(id+"F0.wireOp",EDGE,"E5.24.3"),sQuery(id+"F0.wireOp",EDGE,"E5.25.0"),sQuery(id+"F0.wireOp",EDGE,"E5.25.1"),sQuery(id+"F0.wireOp",EDGE,"E5.25.2"),sQuery(id+"F0.wireOp",EDGE,"E5.25.3"),sQuery(id+"F0.wireOp",EDGE,"E5.26.0"),sQuery(id+"F0.wireOp",EDGE,"E5.26.1"),sQuery(id+"F0.wireOp",EDGE,"E5.26.2"),sQuery(id+"F0.wireOp",EDGE,"E5.26.3"),sQuery(id+"F0.wireOp",EDGE,"E5.27.0"),sQuery(id+"F0.wireOp",EDGE,"E5.27.1"),sQuery(id+"F0.wireOp",EDGE,"E5.27.2"),sQuery(id+"F0.wireOp",EDGE,"E5.27.3"),sQuery(id+"F0.wireOp",EDGE,"E5.28.0"),sQuery(id+"F0.wireOp",EDGE,"E5.28.1"),sQuery(id+"F0.wireOp",EDGE,"E5.28.2"),sQuery(id+"F0.wireOp",EDGE,"E5.28.3"),sQuery(id+"F0.wireOp",EDGE,"E5.29.0"),sQuery(id+"F0.wireOp",EDGE,"E5.29.1"),sQuery(id+"F0.wireOp",EDGE,"E5.29.2"),sQuery(id+"F0.wireOp",EDGE,"E5.29.3"),sQuery(id+"F0.wireOp",EDGE,"E5.30.0"),sQuery(id+"F0.wireOp",EDGE,"E5.30.1"),sQuery(id+"F0.wireOp",EDGE,"E5.30.2"),sQuery(id+"F0.wireOp",EDGE,"E5.30.3"),sQuery(id+"F0.wireOp",EDGE,"E5.31.0"),sQuery(id+"F0.wireOp",EDGE,"E5.31.1"),sQuery(id+"F0.wireOp",EDGE,"E5.31.2"),sQuery(id+"F0.wireOp",EDGE,"E5.31.3"),sQuery(id+"F0.wireOp",EDGE,"E5.32.0"),sQuery(id+"F0.wireOp",EDGE,"E5.32.1"),sQuery(id+"F0.wireOp",EDGE,"E5.32.2"),sQuery(id+"F0.wireOp",EDGE,"E5.32.3"),sQuery(id+"F0.wireOp",EDGE,"E5.33.0"),sQuery(id+"F0.wireOp",EDGE,"E5.33.1"),sQuery(id+"F0.wireOp",EDGE,"E5.33.2"),sQuery(id+"F0.wireOp",EDGE,"E5.33.3"),sQuery(id+"F0.wireOp",EDGE,"E5.34.0"),sQuery(id+"F0.wireOp",EDGE,"E5.34.1"),sQuery(id+"F0.wireOp",EDGE,"E5.34.2"),sQuery(id+"F0.wireOp",EDGE,"E5.34.3"),sQuery(id+"F0.wireOp",EDGE,"E5.35.0"),sQuery(id+"F0.wireOp",EDGE,"E5.35.1"),sQuery(id+"F0.wireOp",EDGE,"E5.35.2"),sQuery(id+"F0.wireOp",EDGE,"E5.35.3"),sQuery(id+"F0.wireOp",EDGE,"E5.36.0"),sQuery(id+"F0.wireOp",EDGE,"E5.36.1"),sQuery(id+"F0.wireOp",EDGE,"E5.36.2"),sQuery(id+"F0.wireOp",EDGE,"E5.36.3"),sQuery(id+"F0.wireOp",EDGE,"E5.37.0"),sQuery(id+"F0.wireOp",EDGE,"E5.37.1"),sQuery(id+"F0.wireOp",EDGE,"E5.37.2"),sQuery(id+"F0.wireOp",EDGE,"E5.37.3"),sQuery(id+"F0.wireOp",EDGE,"E5.38.0"),sQuery(id+"F0.wireOp",EDGE,"E5.38.1"),sQuery(id+"F0.wireOp",EDGE,"E5.38.2"),sQuery(id+"F0.wireOp",EDGE,"E5.38.3"),sQuery(id+"F0.wireOp",EDGE,"E5.39.0"),sQuery(id+"F0.wireOp",EDGE,"E5.39.1"),sQuery(id+"F0.wireOp",EDGE,"E5.39.2"),sQuery(id+"F0.wireOp",EDGE,"E5.39.3"),sQuery(id+"F0.wireOp",EDGE,"E5.40.0"),sQuery(id+"F0.wireOp",EDGE,"E5.40.1"),sQuery(id+"F0.wireOp",EDGE,"E5.40.2"),sQuery(id+"F0.wireOp",EDGE,"E5.40.3"),sQuery(id+"F0.wireOp",EDGE,"E5.41.0"),sQuery(id+"F0.wireOp",EDGE,"E5.41.1"),sQuery(id+"F0.wireOp",EDGE,"E5.41.2"),sQuery(id+"F0.wireOp",EDGE,"E5.41.3"),sQuery(id+"F0.wireOp",EDGE,"E5.42.0"),sQuery(id+"F0.wireOp",EDGE,"E5.42.1"),sQuery(id+"F0.wireOp",EDGE,"E5.42.2"),sQuery(id+"F0.wireOp",EDGE,"E5.42.3"),sQuery(id+"F0.wireOp",EDGE,"E5.43.0"),sQuery(id+"F0.wireOp",EDGE,"E5.43.1"),sQuery(id+"F0.wireOp",EDGE,"E5.43.2"),sQuery(id+"F0.wireOp",EDGE,"E5.43.3"),sQuery(id+"F0.wireOp",EDGE,"E5.44.0"),sQuery(id+"F0.wireOp",EDGE,"E5.44.1"),sQuery(id+"F0.wireOp",EDGE,"E5.44.2"),sQuery(id+"F0.wireOp",EDGE,"E5.44.3"),sQuery(id+"F0.wireOp",EDGE,"E5.45.0"),sQuery(id+"F0.wireOp",EDGE,"E5.45.1"),sQuery(id+"F0.wireOp",EDGE,"E5.45.2"),sQuery(id+"F0.wireOp",EDGE,"E5.45.3"),sQuery(id+"F0.wireOp",EDGE,"E5.46.0"),sQuery(id+"F0.wireOp",EDGE,"E5.46.1"),sQuery(id+"F0.wireOp",EDGE,"E5.46.2"),sQuery(id+"F0.wireOp",EDGE,"E5.46.3"),sQuery(id+"F0.wireOp",EDGE,"E5.47.0"),sQuery(id+"F0.wireOp",EDGE,"E5.47.1"),sQuery(id+"F0.wireOp",EDGE,"E5.47.2"),sQuery(id+"F0.wireOp",EDGE,"E5.47.3"),sQuery(id+"F0.wireOp",EDGE,"E5.48.0"),sQuery(id+"F0.wireOp",EDGE,"E5.48.1"),sQuery(id+"F0.wireOp",EDGE,"E5.48.2"),sQuery(id+"F0.wireOp",EDGE,"E5.48.3"),sQuery(id+"F0.wireOp",EDGE,"E5.49.0"),sQuery(id+"F0.wireOp",EDGE,"E5.49.1"),sQuery(id+"F0.wireOp",EDGE,"E5.49.2"),sQuery(id+"F0.wireOp",EDGE,"E5.49.3"),sQuery(id+"F0.wireOp",EDGE,"E5.50.0"),sQuery(id+"F0.wireOp",EDGE,"E5.50.1"),sQuery(id+"F0.wireOp",EDGE,"E5.50.2"),sQuery(id+"F0.wireOp",EDGE,"E5.50.3"),sQuery(id+"F0.wireOp",EDGE,"E5.51.0"),sQuery(id+"F0.wireOp",EDGE,"E5.51.1"),sQuery(id+"F0.wireOp",EDGE,"E5.51.2"),sQuery(id+"F0.wireOp",EDGE,"E5.51.3"),sQuery(id+"F0.wireOp",EDGE,"E5.52.0"),sQuery(id+"F0.wireOp",EDGE,"E5.52.1"),sQuery(id+"F0.wireOp",EDGE,"E5.52.2"),sQuery(id+"F0.wireOp",EDGE,"E5.52.3"),sQuery(id+"F0.wireOp",EDGE,"E5.53.0"),sQuery(id+"F0.wireOp",EDGE,"E5.53.1"),sQuery(id+"F0.wireOp",EDGE,"E5.53.2"),sQuery(id+"F0.wireOp",EDGE,"E5.53.3"),sQuery(id+"F0.wireOp",EDGE,"E5.54.0"),sQuery(id+"F0.wireOp",EDGE,"E5.54.1"),sQuery(id+"F0.wireOp",EDGE,"E5.54.2"),sQuery(id+"F0.wireOp",EDGE,"E5.54.3"),sQuery(id+"F0.wireOp",EDGE,"E5.55.0"),sQuery(id+"F0.wireOp",EDGE,"E5.55.1"),sQuery(id+"F0.wireOp",EDGE,"E5.55.2"),sQuery(id+"F0.wireOp",EDGE,"E5.55.3"),sQuery(id+"F0.wireOp",EDGE,"E5.56.0"),sQuery(id+"F0.wireOp",EDGE,"E5.56.1"),sQuery(id+"F0.wireOp",EDGE,"E5.56.2"),sQuery(id+"F0.wireOp",EDGE,"E5.56.3"),sQuery(id+"F0.wireOp",EDGE,"E5.57.0"),sQuery(id+"F0.wireOp",EDGE,"E5.57.1"),sQuery(id+"F0.wireOp",EDGE,"E5.57.2"),sQuery(id+"F0.wireOp",EDGE,"E5.57.3"),sQuery(id+"F0.wireOp",EDGE,"E5.58.0"),sQuery(id+"F0.wireOp",EDGE,"E5.58.1"),sQuery(id+"F0.wireOp",EDGE,"E5.58.2"),sQuery(id+"F0.wireOp",EDGE,"E5.58.3"),sQuery(id+"F0.wireOp",EDGE,"E5.59.0"),sQuery(id+"F0.wireOp",EDGE,"E5.59.1"),sQuery(id+"F0.wireOp",EDGE,"E5.59.2"),sQuery(id+"F0.wireOp",EDGE,"E5.59.3")])]});
            var Q1;
            Q1=qCreatedBy(makeId("Front.planeOp"),FACE);
            mirror(context, id + "F7", {"operationType" : NewBodyOperationType.ADD, "entities" : qUnion([Q0]), "mirrorPlane" : qUnion([Q1])});
        }
        {
            var Q0;
            Q0=makeQuery(id+"F6.opExtrude","CAP_FACE",FACE,{"disambiguationData":[OSD([sQuery(id+"F5.wireOp",EDGE,"E7")])],"isStart":false});
            var sketch = newSketch(context, id + "F8", { "sketchPlane" : qUnion([Q0])});
            skCircle(sketch, "E8", {"center": v(0, 0) * mm, "radius": 11.12 * mm});
            skLineSegment(sketch, "E9", {"start": v(0, 0) * mm, "end": v(0, 11.12) * mm, "construction": true});
            skLineSegment(sketch, "E10.bottom", {"start": v(0, 11.12) * mm, "end": v(-2.75, 11.12) * mm});
            skLineSegment(sketch, "E10.top", {"start": v(0, 8.12) * mm, "end": v(-2.75, 8.12) * mm});
            skLineSegment(sketch, "E10.left", {"start": v(0, 11.12) * mm, "end": v(0, 8.12) * mm});
            skLineSegment(sketch, "E10.right", {"start": v(-2.75, 11.12) * mm, "end": v(-2.75, 8.12) * mm});
            skLineSegment(sketch, "E11.MirrorCS", {"start": v(2.75, 11.12) * mm, "end": v(2.75, 8.12) * mm});
            skLineSegment(sketch, "E12.MirrorCS", {"start": v(0, 8.12) * mm, "end": v(2.75, 8.12) * mm});
            skSolve(sketch);
        }
        {
            var Q0;
            {var subQ1=sQuery(id+"F8.wireOp",EDGE,"E10.top");Q0=makeQuery(id+"F8.imprint","IMPRINT",FACE,{"disambiguationData":[TD([[makeQuery(id+"F8.imprint","IMPRINT",EDGE,{"derivedFrom":subQ1}),1.0]])]});}
            extrude(context, id + "F9", {"entities" : qUnion([Q0]), "operationType" : NewBodyOperationType.ADD, "depth" : 70 * mm});
        }
        {
            var Q0;
            Q0=makeQuery(id+"F9.opExtrude","CAP_EDGE",EDGE,{"disambiguationData":[OSD([sQuery(id+"F8.wireOp",EDGE,"E8")])],"isStart":false});
            fillet(context, id + "F10", {"entities" : qUnion([Q0]), "radius" : 1 * mm, "tangentPropagation" : true, "allowEdgeOverflow" : false});
        }
        {
            var Q0;
            Q0=makeQuery(id+"F7.opPattern","COPY",EDGE,{"derivedFrom":makeQuery(id+"F6.opExtrude","CAP_EDGE",EDGE,{"disambiguationData":[OSD([sQuery(id+"F5.wireOp",EDGE,"E7")])],"isStart":false}),"instanceName":"1"});
            fillet(context, id + "F11", {"entities" : qUnion([Q0]), "radius" : 1 * mm, "tangentPropagation" : true, "allowEdgeOverflow" : false});
        }
    });
